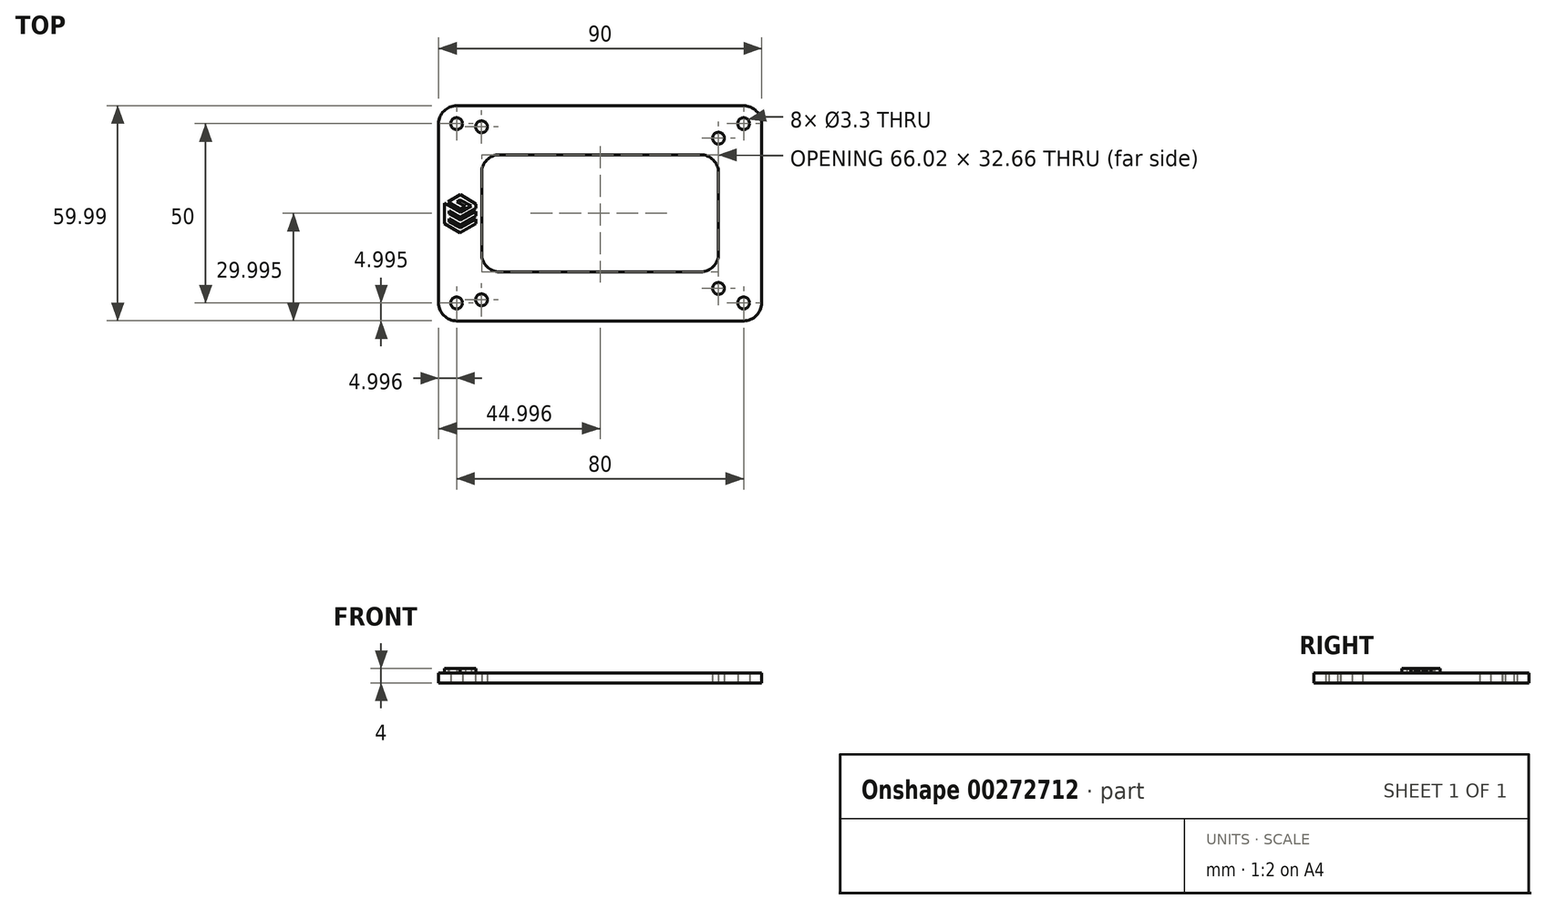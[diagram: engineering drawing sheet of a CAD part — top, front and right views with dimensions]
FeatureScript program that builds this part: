
annotation { "Feature Type Name" : "Feature", "Feature Type Description" : "" }
export const myFeature = defineFeature(function(context is Context, id is Id, definition is map)
    precondition{}
    {
        {
            var Q0;
            Q0=qCreatedBy(makeId("Top.planeOp"),FACE);
            var sketch = newSketch(context, id + "F0", { "sketchPlane" : qUnion([Q0])});
            skCircle(sketch, "E0", {"center": v(14.6, 3.18) * mm, "radius": 1.65 * mm});
            skCircle(sketch, "E1", {"center": v(14.6, 51.44) * mm, "radius": 1.65 * mm});
            skCircle(sketch, "E2", {"center": v(80.65, 48.26) * mm, "radius": 1.65 * mm});
            skCircle(sketch, "E3", {"center": v(80.65, 6.35) * mm, "radius": 1.65 * mm});
            skLineSegment(sketch, "E4.bottom", {"start": v(87.66, 52.3) * mm, "end": v(7.66, 52.3) * mm});
            skCircle(sketch, "E5", {"center": v(7.66, 52.3) * mm, "radius": 1.65 * mm});
            skCircle(sketch, "E6", {"center": v(87.66, 52.3) * mm, "radius": 1.65 * mm});
            skCircle(sketch, "E7", {"center": v(87.66, 2.3) * mm, "radius": 1.65 * mm});
            skCircle(sketch, "E8", {"center": v(7.66, 2.3) * mm, "radius": 1.65 * mm});
            skLineSegment(sketch, "E9.bottom", {"start": v(87.66, 57.3) * mm, "end": v(7.66, 57.3) * mm});
            skLineSegment(sketch, "E9.top", {"start": v(87.66, -2.7) * mm, "end": v(7.66, -2.7) * mm});
            skLineSegment(sketch, "E9.left", {"start": v(92.66, 52.3) * mm, "end": v(92.66, 2.3) * mm});
            skLineSegment(sketch, "E9.right", {"start": v(2.66, 52.3) * mm, "end": v(2.66, 2.3) * mm});
            skLineSegment(sketch, "E10.bottom", {"start": v(75.67, 43.64) * mm, "end": v(19.65, 43.64) * mm});
            skLineSegment(sketch, "E10.top", {"start": v(75.67, 10.97) * mm, "end": v(19.65, 10.97) * mm});
            skLineSegment(sketch, "E10.left", {"start": v(80.67, 38.64) * mm, "end": v(80.67, 15.97) * mm});
            skLineSegment(sketch, "E10.right", {"start": v(14.65, 38.64) * mm, "end": v(14.65, 15.97) * mm});
            skPoint(sketch, "E10.middle", {"position": v(47.66, 27.3) * mm});
            skPoint(sketch, "E11.visualSharp", {"position": v(2.66, 57.3) * mm});
            skArc(sketch, "E11.filletArc", {"start": v(7.66, 57.3) * mm, "mid": v(4.12, 55.84) * mm, "end": v(2.66, 52.3) * mm});
            skPoint(sketch, "E12.visualSharp", {"position": v(2.66, -2.7) * mm});
            skArc(sketch, "E12.filletArc", {"start": v(2.66, 2.3) * mm, "mid": v(4.12, -1.23) * mm, "end": v(7.66, -2.7) * mm});
            skPoint(sketch, "E13.visualSharp", {"position": v(92.66, -2.7) * mm});
            skArc(sketch, "E13.filletArc", {"start": v(87.66, -2.7) * mm, "mid": v(91.2, -1.23) * mm, "end": v(92.66, 2.3) * mm});
            skPoint(sketch, "E14.visualSharp", {"position": v(92.66, 57.3) * mm});
            skArc(sketch, "E14.filletArc", {"start": v(92.66, 52.3) * mm, "mid": v(91.2, 55.84) * mm, "end": v(87.66, 57.3) * mm});
            skPoint(sketch, "E15.visualSharp", {"position": v(80.67, 43.64) * mm});
            skArc(sketch, "E15.filletArc", {"start": v(80.67, 38.64) * mm, "mid": v(79.2, 42.17) * mm, "end": v(75.67, 43.64) * mm});
            skPoint(sketch, "E16.visualSharp", {"position": v(14.65, 10.97) * mm});
            skArc(sketch, "E16.filletArc", {"start": v(14.65, 15.97) * mm, "mid": v(16.11, 12.44) * mm, "end": v(19.65, 10.97) * mm});
            skPoint(sketch, "E17.visualSharp", {"position": v(80.67, 10.97) * mm});
            skArc(sketch, "E17.filletArc", {"start": v(75.67, 10.97) * mm, "mid": v(79.2, 12.44) * mm, "end": v(80.67, 15.97) * mm});
            skPoint(sketch, "E18.visualSharp", {"position": v(14.65, 43.64) * mm});
            skArc(sketch, "E18.filletArc", {"start": v(19.65, 43.64) * mm, "mid": v(16.11, 42.17) * mm, "end": v(14.65, 38.64) * mm});
            skLineSegment(sketch, "E19", {"start": v(13.06, 25.7) * mm, "end": v(13.06, 24.39) * mm});
            skLineSegment(sketch, "E20", {"start": v(13.06, 24.39) * mm, "end": v(8.65, 21.85) * mm});
            skLineSegment(sketch, "E21", {"start": v(8.65, 21.85) * mm, "end": v(4.25, 24.39) * mm});
            skLineSegment(sketch, "E22", {"start": v(4.25, 24.39) * mm, "end": v(4.25, 30.07) * mm});
            skLineSegment(sketch, "E23", {"start": v(4.25, 30.07) * mm, "end": v(8.68, 27.64) * mm});
            skLineSegment(sketch, "E24", {"start": v(8.68, 27.64) * mm, "end": v(11.75, 29.37) * mm});
            skLineSegment(sketch, "E25", {"start": v(11.75, 29.37) * mm, "end": v(8.65, 31.07) * mm});
            skLineSegment(sketch, "E26", {"start": v(8.65, 31.07) * mm, "end": v(7.71, 30.57) * mm});
            skLineSegment(sketch, "E27", {"start": v(7.71, 30.57) * mm, "end": v(10.07, 29.18) * mm});
            skLineSegment(sketch, "E28", {"start": v(10.07, 29.18) * mm, "end": v(8.81, 28.5) * mm});
            skLineSegment(sketch, "E29", {"start": v(8.81, 28.5) * mm, "end": v(5.3, 30.57) * mm});
            skLineSegment(sketch, "E30", {"start": v(5.3, 30.57) * mm, "end": v(8.68, 32.48) * mm});
            skLineSegment(sketch, "E31", {"start": v(8.68, 32.48) * mm, "end": v(13.06, 29.94) * mm});
            skLineSegment(sketch, "E32", {"start": v(13.06, 29.94) * mm, "end": v(13.06, 28.76) * mm});
            skLineSegment(sketch, "E33", {"start": v(13.06, 28.76) * mm, "end": v(8.65, 26.22) * mm});
            skLineSegment(sketch, "E34", {"start": v(8.65, 26.22) * mm, "end": v(5.56, 27.95) * mm});
            skLineSegment(sketch, "E35", {"start": v(5.56, 27.95) * mm, "end": v(5.56, 27.17) * mm});
            skLineSegment(sketch, "E36", {"start": v(5.56, 27.17) * mm, "end": v(8.68, 25.46) * mm});
            skLineSegment(sketch, "E37", {"start": v(8.68, 25.46) * mm, "end": v(13.06, 27.87) * mm});
            skLineSegment(sketch, "E38", {"start": v(13.06, 27.87) * mm, "end": v(13.06, 26.56) * mm});
            skLineSegment(sketch, "E39", {"start": v(13.06, 26.56) * mm, "end": v(8.65, 24.05) * mm});
            skLineSegment(sketch, "E40", {"start": v(8.65, 24.05) * mm, "end": v(5.56, 25.8) * mm});
            skLineSegment(sketch, "E41", {"start": v(5.56, 25.8) * mm, "end": v(5.56, 25) * mm});
            skLineSegment(sketch, "E42", {"start": v(5.56, 25) * mm, "end": v(8.68, 23.26) * mm});
            skLineSegment(sketch, "E43", {"start": v(8.68, 23.26) * mm, "end": v(13.06, 25.7) * mm});
            skSolve(sketch);
        }
        {
            var Q0;
            Q0 = qSketchRegion(id + "F0", true);
            var Q1;
            Q1=makeQuery(id+"F0.imprint","IMPRINT",FACE,{"disambiguationData":[TD([[makeQuery(id+"F0.imprint","IMPRINT",EDGE,{"derivedFrom":sQuery(id+"F0.wireOp",EDGE,"E19")}),-1.0]])]});
            extrude(context, id + "F1", {"entities" : qUnion([Q0, Q1]), "depth" : 2.8 * mm});
        }
        {
            var Q0;
            Q0=makeQuery(id+"F0.imprint","IMPRINT",FACE,{"disambiguationData":[TD([[makeQuery(id+"F0.imprint","IMPRINT",EDGE,{"derivedFrom":sQuery(id+"F0.wireOp",EDGE,"E19")}),-1.0]])]});
            extrude(context, id + "F2", {"entities" : qUnion([Q0]), "operationType" : NewBodyOperationType.ADD, "depth" : 4 * mm});
        }
    });
